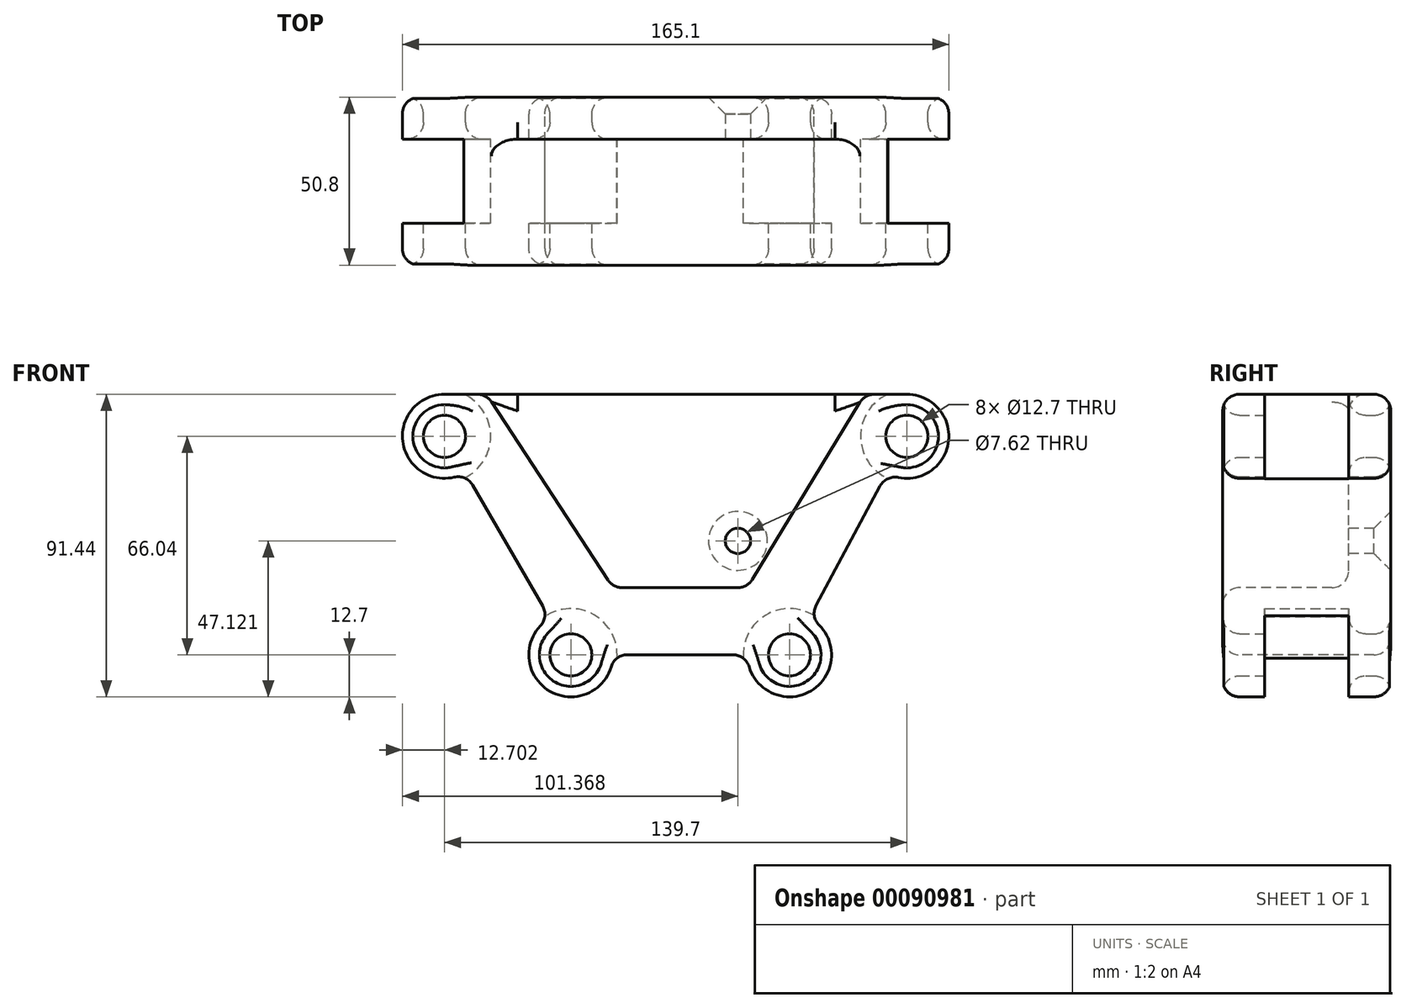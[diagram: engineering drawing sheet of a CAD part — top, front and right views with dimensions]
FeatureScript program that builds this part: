
annotation { "Feature Type Name" : "Feature", "Feature Type Description" : "" }
export const myFeature = defineFeature(function(context is Context, id is Id, definition is map)
    precondition{}
    {
        {
            var Q0;
            Q0=qCreatedBy(makeId("Front.planeOp"),FACE);
            var sketch = newSketch(context, id + "F0", { "sketchPlane" : qUnion([Q0])});
            skLineSegment(sketch, "E0", {"start": v(-31.21, -66.04) * mm, "end": v(34.83, -66.04) * mm});
            skLineSegment(sketch, "E1", {"start": v(34.83, -66.04) * mm, "end": v(70.3, 0) * mm});
            skLineSegment(sketch, "E2", {"start": v(-31.21, -66.04) * mm, "end": v(-69.4, 0) * mm});
            skCircle(sketch, "E3", {"center": v(-69.4, 0) * mm, "radius": 6.35 * mm});
            skCircle(sketch, "E4", {"center": v(-31.21, -66.04) * mm, "radius": 6.35 * mm});
            skCircle(sketch, "E5", {"center": v(34.83, -66.04) * mm, "radius": 6.35 * mm});
            skCircle(sketch, "E6", {"center": v(70.3, 0) * mm, "radius": 6.35 * mm});
            skCircle(sketch, "E7", {"center": v(-69.4, 0) * mm, "radius": 12.7 * mm});
            skCircle(sketch, "E8", {"center": v(-31.21, -66.04) * mm, "radius": 12.7 * mm});
            skCircle(sketch, "E9", {"center": v(34.83, -66.04) * mm, "radius": 12.7 * mm});
            skCircle(sketch, "E10", {"center": v(70.3, 0) * mm, "radius": 12.7 * mm});
            skLineSegment(sketch, "E11", {"start": v(-69.4, 12.7) * mm, "end": v(70.3, 12.7) * mm});
            skLineSegment(sketch, "E12", {"start": v(1.8, -66.04) * mm, "end": v(1.8, -31.77) * mm, "construction": true});
            skPoint(sketch, "E13", {"position": v(1.8, 12.7) * mm});
            skSolve(sketch);
        }
        {
            var Q0;
            Q0 = qSketchRegion(id + "F0", true);
            extrude(context, id + "F1", {"entities" : qUnion([Q0]), "endBound" : BoundingType.SYMMETRIC, "depth" : 50.8 * mm});
        }
        {
            var Q0;
            Q0=makeQuery(id+"F1.opExtrude","CAP_FACE",FACE,{"disambiguationData":[OSD([sQuery(id+"F0.wireOp",EDGE,"E0"),sQuery(id+"F0.wireOp",EDGE,"E1"),sQuery(id+"F0.wireOp",EDGE,"E2"),sQuery(id+"F0.wireOp",EDGE,"E3"),sQuery(id+"F0.wireOp",EDGE,"E4"),sQuery(id+"F0.wireOp",EDGE,"E5"),sQuery(id+"F0.wireOp",EDGE,"E6"),sQuery(id+"F0.wireOp",EDGE,"E7"),sQuery(id+"F0.wireOp",EDGE,"E8"),sQuery(id+"F0.wireOp",EDGE,"E9"),sQuery(id+"F0.wireOp",EDGE,"E10"),sQuery(id+"F0.wireOp",EDGE,"E11")])],"isStart":false});
            var sketch = newSketch(context, id + "F2", { "sketchPlane" : qUnion([Q0])});
            skLineSegment(sketch, "E14", {"start": v(-18.51, -45.72) * mm, "end": v(22.13, -45.72) * mm});
            skLineSegment(sketch, "E15", {"start": v(22.13, -45.72) * mm, "end": v(57.6, 12.7) * mm});
            skLineSegment(sketch, "E16", {"start": v(57.6, 12.7) * mm, "end": v(-56.7, 12.7) * mm});
            skLineSegment(sketch, "E17", {"start": v(-56.7, 12.7) * mm, "end": v(-18.51, -45.72) * mm});
            skSolve(sketch);
        }
        {
            var Q0;
            Q0 = qSketchRegion(id + "F2", true);
            extrude(context, id + "F3", {"entities" : qUnion([Q0]), "operationType" : NewBodyOperationType.REMOVE, "oppositeDirection" : true, "depth" : 38.1 * mm});
        }
        {
            var Q0;
            Q0=makeQuery(id+"F1.opExtrude","SWEPT_FACE",FACE,{"disambiguationData":[OSD([sQuery(id+"F0.wireOp",EDGE,"E1")])]});
            var Q1;
            Q1=makeQuery(id+"F1.opExtrude","SWEPT_FACE",FACE,{"disambiguationData":[OSD([sQuery(id+"F0.wireOp",EDGE,"E2")])]});
            var Q2;
            Q2=makeQuery(id+"F1.opExtrude","SWEPT_FACE",FACE,{"disambiguationData":[OSD([sQuery(id+"F0.wireOp",EDGE,"E5")])]});
            var Q3;
            Q3=makeQuery(id+"F1.opExtrude","CAP_EDGE",EDGE,{"disambiguationData":[OSD([sQuery(id+"F0.wireOp",EDGE,"E6")])],"isStart":false});
            var Q4;
            Q4=makeQuery(id+"F1.opExtrude","SWEPT_FACE",FACE,{"disambiguationData":[OSD([sQuery(id+"F0.wireOp",EDGE,"E8")])]});
            var Q5;
            Q5=makeQuery(id+"F1.opExtrude","CAP_EDGE",EDGE,{"disambiguationData":[OSD([sQuery(id+"F0.wireOp",EDGE,"E9")])],"isStart":true});
            var Q6;
            Q6=makeQuery(id+"F3.boolean.opBoolean","COPY",EDGE,{"derivedFrom":makeQuery(id+"F3.opExtrude","CAP_EDGE",EDGE,{"disambiguationData":[OSD([sQuery(id+"F2.wireOp",EDGE,"E17")])],"isStart":false})});
            var Q7;
            Q7=makeQuery(id+"F3.boolean.opBoolean","COPY",EDGE,{"derivedFrom":makeQuery(id+"F3.opExtrude","CAP_EDGE",EDGE,{"disambiguationData":[OSD([sQuery(id+"F2.wireOp",EDGE,"E17")])],"isStart":true})});
            var Q8;
            Q8=makeQuery(id+"F1.opExtrude","CAP_EDGE",EDGE,{"disambiguationData":[OSD([sQuery(id+"F0.wireOp",EDGE,"E8")])],"isStart":false});
            var Q9;
            Q9=makeQuery(id+"F1.opExtrude","SWEPT_FACE",FACE,{"disambiguationData":[OSD([sQuery(id+"F0.wireOp",EDGE,"E9")])]});
            var Q10;
            Q10=makeQuery(id+"F1.opExtrude","CAP_EDGE",EDGE,{"disambiguationData":[OSD([sQuery(id+"F0.wireOp",EDGE,"E10")])],"isStart":false});
            var Q11;
            Q11=makeQuery(id+"F3.boolean.opBoolean","COPY",FACE,{"derivedFrom":makeQuery(id+"F3.opExtrude","SWEPT_FACE",FACE,{"disambiguationData":[OSD([sQuery(id+"F2.wireOp",EDGE,"E14")])]})});
            var Q12;
            Q12=makeQuery(id+"F1.opExtrude","CAP_EDGE",EDGE,{"disambiguationData":[OSD([sQuery(id+"F0.wireOp",EDGE,"E2")])],"isStart":false});
            var Q13;
            Q13=makeQuery(id+"F1.opExtrude","CAP_EDGE",EDGE,{"disambiguationData":[OSD([sQuery(id+"F0.wireOp",EDGE,"E5")])],"isStart":false});
            var Q14;
            Q14=makeQuery(id+"F1.opExtrude","CAP_EDGE",EDGE,{"disambiguationData":[OSD([sQuery(id+"F0.wireOp",EDGE,"E1")])],"isStart":true});
            var Q15;
            Q15=makeQuery(id+"F3.boolean.opBoolean","COPY",FACE,{"derivedFrom":makeQuery(id+"F3.opExtrude","CAP_FACE",FACE,{"disambiguationData":[OSD([sQuery(id+"F2.wireOp",EDGE,"E14"),sQuery(id+"F2.wireOp",EDGE,"E15"),sQuery(id+"F2.wireOp",EDGE,"E16"),sQuery(id+"F2.wireOp",EDGE,"E17")])],"isStart":false})});
            var Q16;
            Q16=makeQuery(id+"F1.opExtrude","SWEPT_FACE",FACE,{"disambiguationData":[OSD([sQuery(id+"F0.wireOp",EDGE,"E6")])]});
            var Q17;
            Q17=makeQuery(id+"F1.opExtrude","SWEPT_FACE",FACE,{"disambiguationData":[OSD([sQuery(id+"F0.wireOp",EDGE,"E3")])]});
            var Q18;
            Q18=makeQuery(id+"F1.opExtrude","CAP_FACE",FACE,{"disambiguationData":[OSD([sQuery(id+"F0.wireOp",EDGE,"E0"),sQuery(id+"F0.wireOp",EDGE,"E1"),sQuery(id+"F0.wireOp",EDGE,"E2"),sQuery(id+"F0.wireOp",EDGE,"E3"),sQuery(id+"F0.wireOp",EDGE,"E4"),sQuery(id+"F0.wireOp",EDGE,"E5"),sQuery(id+"F0.wireOp",EDGE,"E6"),sQuery(id+"F0.wireOp",EDGE,"E7"),sQuery(id+"F0.wireOp",EDGE,"E8"),sQuery(id+"F0.wireOp",EDGE,"E9"),sQuery(id+"F0.wireOp",EDGE,"E10"),sQuery(id+"F0.wireOp",EDGE,"E11")])],"isStart":true});
            var Q19;
            Q19=makeQuery(id+"F1.opExtrude","CAP_EDGE",EDGE,{"disambiguationData":[OSD([sQuery(id+"F0.wireOp",EDGE,"E3")])],"isStart":false});
            var Q20;
            Q20=makeQuery(id+"F1.opExtrude","SWEPT_FACE",FACE,{"disambiguationData":[OSD([sQuery(id+"F0.wireOp",EDGE,"E7")])]});
            var Q21;
            Q21=makeQuery(id+"F1.opExtrude","CAP_EDGE",EDGE,{"disambiguationData":[OSD([sQuery(id+"F0.wireOp",EDGE,"E4")])],"isStart":false});
            var Q22;
            Q22=makeQuery(id+"F1.opExtrude","SWEPT_FACE",FACE,{"disambiguationData":[OSD([sQuery(id+"F0.wireOp",EDGE,"E4")])]});
            var Q23;
            Q23=makeQuery(id+"F1.opExtrude","SWEPT_FACE",FACE,{"disambiguationData":[OSD([sQuery(id+"F0.wireOp",EDGE,"E0")])]});
            var Q24;
            Q24=makeQuery(id+"F3.boolean.opBoolean","COPY",EDGE,{"derivedFrom":makeQuery(id+"F3.opExtrude","SWEPT_EDGE",EDGE,{"disambiguationData":[OSD([sQuery(id+"F0.wireOp",EDGE,"E11"),sQuery(id+"F2.wireOp",EDGE,"E16"),sQuery(id+"F2.wireOp",EDGE,"E17")])]})});
            var Q25;
            Q25=makeQuery(id+"F1.opExtrude","CAP_EDGE",EDGE,{"disambiguationData":[OSD([sQuery(id+"F0.wireOp",EDGE,"E9")])],"isStart":false});
            var Q26;
            Q26=makeQuery(id+"F1.opExtrude","CAP_EDGE",EDGE,{"disambiguationData":[OSD([sQuery(id+"F0.wireOp",EDGE,"E10")])],"isStart":true});
            var Q27;
            Q27=makeQuery(id+"F1.opExtrude","SWEPT_FACE",FACE,{"disambiguationData":[OSD([sQuery(id+"F0.wireOp",EDGE,"E10")])]});
            var Q28;
            Q28=makeQuery(id+"F1.opExtrude","CAP_FACE",FACE,{"disambiguationData":[OSD([sQuery(id+"F0.wireOp",EDGE,"E0"),sQuery(id+"F0.wireOp",EDGE,"E1"),sQuery(id+"F0.wireOp",EDGE,"E2"),sQuery(id+"F0.wireOp",EDGE,"E3"),sQuery(id+"F0.wireOp",EDGE,"E4"),sQuery(id+"F0.wireOp",EDGE,"E5"),sQuery(id+"F0.wireOp",EDGE,"E6"),sQuery(id+"F0.wireOp",EDGE,"E7"),sQuery(id+"F0.wireOp",EDGE,"E8"),sQuery(id+"F0.wireOp",EDGE,"E9"),sQuery(id+"F0.wireOp",EDGE,"E10"),sQuery(id+"F0.wireOp",EDGE,"E11")])],"isStart":false});
            var Q29;
            Q29=makeQuery(id+"F3.boolean.opBoolean","COPY",FACE,{"derivedFrom":makeQuery(id+"F3.opExtrude","SWEPT_FACE",FACE,{"disambiguationData":[OSD([sQuery(id+"F2.wireOp",EDGE,"E15")])]})});
            var Q30;
            Q30=makeQuery(id+"F3.boolean.opBoolean","COPY",EDGE,{"derivedFrom":makeQuery(id+"F3.opExtrude","CAP_EDGE",EDGE,{"disambiguationData":[OSD([sQuery(id+"F2.wireOp",EDGE,"E15")])],"isStart":true})});
            var Q31;
            Q31=makeQuery(id+"F3.boolean.opBoolean","COPY",EDGE,{"derivedFrom":makeQuery(id+"F3.opExtrude","CAP_EDGE",EDGE,{"disambiguationData":[OSD([sQuery(id+"F2.wireOp",EDGE,"E16")])],"isStart":false})});
            var Q32;
            Q32=makeQuery(id+"F1.opExtrude","SWEPT_FACE",FACE,{"disambiguationData":[OSD([sQuery(id+"F0.wireOp",EDGE,"E11")])]});
            var Q33;
            Q33=makeQuery(id+"F1.opExtrude","CAP_EDGE",EDGE,{"disambiguationData":[OSD([sQuery(id+"F0.wireOp",EDGE,"E7")])],"isStart":false});
            var Q34;
            Q34=makeQuery(id+"F1.opExtrude","CAP_EDGE",EDGE,{"disambiguationData":[OSD([sQuery(id+"F0.wireOp",EDGE,"E1")])],"isStart":false});
            var Q35;
            Q35=makeQuery(id+"F3.boolean.opBoolean","COPY",FACE,{"derivedFrom":makeQuery(id+"F3.opExtrude","SWEPT_FACE",FACE,{"disambiguationData":[OSD([sQuery(id+"F2.wireOp",EDGE,"E17")])]})});
            var Q36;
            Q36=makeQuery(id+"F1.opExtrude","SWEPT_EDGE",EDGE,{"disambiguationData":[OSD([sQuery(id+"F0.wireOp",EDGE,"E10"),sQuery(id+"F0.wireOp",EDGE,"E11")])]});
            var Q37;
            Q37=makeQuery(id+"F1.opExtrude","SWEPT_EDGE",EDGE,{"disambiguationData":[OSD([sQuery(id+"F0.wireOp",EDGE,"E1"),sQuery(id+"F0.wireOp",EDGE,"E10")])]});
            var Q38;
            Q38=makeQuery(id+"F1.opExtrude","CAP_EDGE",EDGE,{"disambiguationData":[OSD([sQuery(id+"F0.wireOp",EDGE,"E4")])],"isStart":true});
            var Q39;
            Q39=makeQuery(id+"F1.opExtrude","CAP_EDGE",EDGE,{"disambiguationData":[OSD([sQuery(id+"F0.wireOp",EDGE,"E6")])],"isStart":true});
            var Q40;
            Q40=makeQuery(id+"F3.boolean.opBoolean","COPY",EDGE,{"derivedFrom":makeQuery(id+"F3.opExtrude","SWEPT_EDGE",EDGE,{"disambiguationData":[OSD([sQuery(id+"F0.wireOp",EDGE,"E11"),sQuery(id+"F2.wireOp",EDGE,"E15"),sQuery(id+"F2.wireOp",EDGE,"E16")])]})});
            var Q41;
            Q41=makeQuery(id+"F1.opExtrude","CAP_EDGE",EDGE,{"disambiguationData":[OSD([sQuery(id+"F0.wireOp",EDGE,"E7")])],"isStart":true});
            var Q42;
            Q42=makeQuery(id+"F3.boolean.opBoolean","COPY",EDGE,{"derivedFrom":makeQuery(id+"F3.opExtrude","SWEPT_EDGE",EDGE,{"disambiguationData":[OSD([sQuery(id+"F2.wireOp",EDGE,"E14"),sQuery(id+"F2.wireOp",EDGE,"E17")])]})});
            var Q43;
            Q43=makeQuery(id+"F1.opExtrude","CAP_EDGE",EDGE,{"disambiguationData":[OSD([sQuery(id+"F0.wireOp",EDGE,"E2")])],"isStart":true});
            var Q44;
            Q44=makeQuery(id+"F1.opExtrude","CAP_EDGE",EDGE,{"disambiguationData":[OSD([sQuery(id+"F0.wireOp",EDGE,"E0")])],"isStart":false});
            var Q45;
            Q45=makeQuery(id+"F1.opExtrude","CAP_EDGE",EDGE,{"disambiguationData":[OSD([sQuery(id+"F0.wireOp",EDGE,"E11")])],"isStart":true});
            var Q46;
            Q46=makeQuery(id+"F1.opExtrude","CAP_EDGE",EDGE,{"disambiguationData":[OSD([sQuery(id+"F0.wireOp",EDGE,"E8")])],"isStart":true});
            var Q47;
            Q47=makeQuery(id+"F1.opExtrude","SWEPT_EDGE",EDGE,{"disambiguationData":[OSD([sQuery(id+"F0.wireOp",EDGE,"E2"),sQuery(id+"F0.wireOp",EDGE,"E7")])]});
            var Q48;
            Q48=makeQuery(id+"F1.opExtrude","SWEPT_EDGE",EDGE,{"disambiguationData":[OSD([sQuery(id+"F0.wireOp",EDGE,"E2"),sQuery(id+"F0.wireOp",EDGE,"E8")])]});
            var Q49;
            Q49=makeQuery(id+"F1.opExtrude","SWEPT_EDGE",EDGE,{"disambiguationData":[OSD([sQuery(id+"F0.wireOp",EDGE,"E7"),sQuery(id+"F0.wireOp",EDGE,"E11")])]});
            var Q50;
            Q50=makeQuery(id+"F1.opExtrude","CAP_EDGE",EDGE,{"disambiguationData":[OSD([sQuery(id+"F0.wireOp",EDGE,"E5")])],"isStart":true});
            var Q51;
            Q51=makeQuery(id+"F1.opExtrude","CAP_EDGE",EDGE,{"disambiguationData":[OSD([sQuery(id+"F0.wireOp",EDGE,"E3")])],"isStart":true});
            var Q52;
            Q52=makeQuery(id+"F1.opExtrude","SWEPT_EDGE",EDGE,{"disambiguationData":[OSD([sQuery(id+"F0.wireOp",EDGE,"E1"),sQuery(id+"F0.wireOp",EDGE,"E9")])]});
            var Q53;
            Q53=makeQuery(id+"F1.opExtrude","SWEPT_EDGE",EDGE,{"disambiguationData":[OSD([sQuery(id+"F0.wireOp",EDGE,"E0"),sQuery(id+"F0.wireOp",EDGE,"E9")])]});
            var Q54;
            Q54=makeQuery(id+"F1.opExtrude","SWEPT_EDGE",EDGE,{"disambiguationData":[OSD([sQuery(id+"F0.wireOp",EDGE,"E0"),sQuery(id+"F0.wireOp",EDGE,"E8")])]});
            var Q55;
            Q55=makeQuery(id+"F3.boolean.opBoolean","COPY",EDGE,{"derivedFrom":makeQuery(id+"F3.opExtrude","CAP_EDGE",EDGE,{"disambiguationData":[OSD([sQuery(id+"F2.wireOp",EDGE,"E15")])],"isStart":false})});
            var Q56;
            {var subQ0=sQuery(id+"F0.wireOp",EDGE,"E11");var subQ1=sQuery(id+"F0.wireOp",EDGE,"E7");Q56=makeQuery(id+"F3.boolean.opBoolean","SPLIT",EDGE,{"disambiguationData":[TD([makeQuery(id+"F1.opExtrude","SWEPT_FACE",FACE,{"disambiguationData":[OSD([subQ1])]})])],"derivedFrom":makeQuery(id+"F1.opExtrude","CAP_EDGE",EDGE,{"disambiguationData":[OSD([subQ0])],"isStart":false})});}
            var Q57;
            Q57=makeQuery(id+"F3.boolean.opBoolean","COPY",EDGE,{"derivedFrom":makeQuery(id+"F3.opExtrude","CAP_EDGE",EDGE,{"disambiguationData":[OSD([sQuery(id+"F2.wireOp",EDGE,"E14")])],"isStart":true})});
            var Q58;
            {var subQ0=sQuery(id+"F0.wireOp",EDGE,"E11");var subQ1=sQuery(id+"F0.wireOp",EDGE,"E10");Q58=makeQuery(id+"F3.boolean.opBoolean","SPLIT",EDGE,{"disambiguationData":[TD([makeQuery(id+"F1.opExtrude","SWEPT_FACE",FACE,{"disambiguationData":[OSD([subQ1])]})])],"derivedFrom":makeQuery(id+"F1.opExtrude","CAP_EDGE",EDGE,{"disambiguationData":[OSD([subQ0])],"isStart":false})});}
            var Q59;
            Q59=makeQuery(id+"F3.boolean.opBoolean","COPY",EDGE,{"derivedFrom":makeQuery(id+"F3.opExtrude","SWEPT_EDGE",EDGE,{"disambiguationData":[OSD([sQuery(id+"F2.wireOp",EDGE,"E14"),sQuery(id+"F2.wireOp",EDGE,"E15")])]})});
            var Q60;
            Q60=makeQuery(id+"F1.opExtrude","CAP_EDGE",EDGE,{"disambiguationData":[OSD([sQuery(id+"F0.wireOp",EDGE,"E0")])],"isStart":true});
            var Q61;
            Q61=makeQuery(id+"F3.boolean.opBoolean","COPY",EDGE,{"derivedFrom":makeQuery(id+"F3.opExtrude","CAP_EDGE",EDGE,{"disambiguationData":[OSD([sQuery(id+"F2.wireOp",EDGE,"E14")])],"isStart":false})});
            fillet(context, id + "F4", {"entities" : qUnion([Q0, Q1, Q2, Q3, Q4, Q5, Q6, Q7, Q8, Q9, Q10, Q11, Q12, Q13, Q14, Q15, Q16, Q17, Q18, Q19, Q20, Q21, Q22, Q23, Q24, Q25, Q26, Q27, Q28, Q29, Q30, Q31, Q32, Q33, Q34, Q35, Q36, Q37, Q38, Q39, Q40, Q41, Q42, Q43, Q44, Q45, Q46, Q47, Q48, Q49, Q50, Q51, Q52, Q53, Q54, Q55, Q56, Q57, Q58, Q59, Q60, Q61]), "radius" : 5.08 * mm, "tangentPropagation" : true, "allowEdgeOverflow" : false});
        }
        {
            var Q0;
            Q0=qCreatedBy(makeId("Front.planeOp"),FACE);
            var sketch = newSketch(context, id + "F5", { "sketchPlane" : qUnion([Q0])});
            skCircle(sketch, "E18.0", {"center": v(-69.4, 0) * mm, "radius": 6.35 * mm});
            skCircle(sketch, "E19.0", {"center": v(70.3, 0) * mm, "radius": 6.35 * mm});
            skCircle(sketch, "E20.0", {"center": v(34.83, -66.04) * mm, "radius": 6.35 * mm});
            skCircle(sketch, "E21.0", {"center": v(-31.21, -66.04) * mm, "radius": 6.35 * mm});
            skCircle(sketch, "E22", {"center": v(-69.4, 0) * mm, "radius": 13.97 * mm});
            skCircle(sketch, "E23", {"center": v(70.3, 0) * mm, "radius": 13.97 * mm});
            skCircle(sketch, "E24", {"center": v(-31.21, -66.04) * mm, "radius": 13.97 * mm});
            skCircle(sketch, "E25", {"center": v(34.83, -66.04) * mm, "radius": 13.97 * mm});
            skSolve(sketch);
        }
        {
            var Q0;
            Q0 = qSketchRegion(id + "F5", true);
            extrude(context, id + "F6", {"entities" : qUnion([Q0]), "operationType" : NewBodyOperationType.REMOVE, "endBound" : BoundingType.SYMMETRIC, "depth" : 25.4 * mm});
        }
        {
            var Q0;
            Q0=makeQuery(id+"F3.boolean.opBoolean","COPY",FACE,{"derivedFrom":makeQuery(id+"F3.opExtrude","CAP_FACE",FACE,{"disambiguationData":[OSD([sQuery(id+"F2.wireOp",EDGE,"E14"),sQuery(id+"F2.wireOp",EDGE,"E15"),sQuery(id+"F2.wireOp",EDGE,"E16"),sQuery(id+"F2.wireOp",EDGE,"E17")])],"isStart":false})});
            var sketch = newSketch(context, id + "F7", { "sketchPlane" : qUnion([Q0])});
            skLineSegment(sketch, "E26", {"start": v(0, -31.62) * mm, "end": v(-27.73, -31.62) * mm});
            skLineSegment(sketch, "E27", {"start": v(-27.73, -31.62) * mm, "end": v(30.69, -31.62) * mm});
            skCircle(sketch, "E28", {"center": v(-16.3, -31.62) * mm, "radius": 3.81 * mm});
            skCircle(sketch, "E29", {"center": v(19.26, -31.62) * mm, "radius": 3.81 * mm});
            skSolve(sketch);
        }
        {
            var Q0;
            {var subQ0=sQuery(id+"F7.wireOp",EDGE,"E28");var subQ1=sQuery(id+"F7.wireOp",EDGE,"E27");var subQ2=makeQuery(id+"F7.imprint","INTERSECT",VERTEX,{"disambiguationData":[OD(0.0)],"derivedFrom":[subQ1,subQ0]});Q0=makeQuery(id+"F7.imprint","IMPRINT",FACE,{"disambiguationData":[TD([[makeQuery(id+"F7.imprint","IMPRINT",EDGE,{"disambiguationData":[TD([[subQ2,-1.0]])],"derivedFrom":subQ1}),-1.0]])]});}
            var Q1;
            {var subQ0=sQuery(id+"F7.wireOp",EDGE,"E29");var subQ1=sQuery(id+"F7.wireOp",EDGE,"E27");var subQ2=makeQuery(id+"F7.imprint","INTERSECT",VERTEX,{"disambiguationData":[OD(0.0)],"derivedFrom":[subQ1,subQ0]});Q1=makeQuery(id+"F7.imprint","IMPRINT",FACE,{"disambiguationData":[TD([[makeQuery(id+"F7.imprint","IMPRINT",EDGE,{"disambiguationData":[TD([[subQ2,-1.0]])],"derivedFrom":subQ1}),-1.0]])]});}
            var Q2;
            {var subQ0=sQuery(id+"F7.wireOp",EDGE,"E28");var subQ1=sQuery(id+"F7.wireOp",EDGE,"E27");var subQ2=makeQuery(id+"F7.imprint","INTERSECT",VERTEX,{"disambiguationData":[OD(0.0)],"derivedFrom":[subQ1,subQ0]});Q2=makeQuery(id+"F7.imprint","IMPRINT",FACE,{"disambiguationData":[TD([[makeQuery(id+"F7.imprint","IMPRINT",EDGE,{"disambiguationData":[TD([[subQ2,-1.0]])],"derivedFrom":subQ1}),1.0]])]});}
            var Q3;
            {var subQ0=sQuery(id+"F7.wireOp",EDGE,"E29");var subQ1=sQuery(id+"F7.wireOp",EDGE,"E27");var subQ2=makeQuery(id+"F7.imprint","INTERSECT",VERTEX,{"disambiguationData":[OD(0.0)],"derivedFrom":[subQ1,subQ0]});Q3=makeQuery(id+"F7.imprint","IMPRINT",FACE,{"disambiguationData":[TD([[makeQuery(id+"F7.imprint","IMPRINT",EDGE,{"disambiguationData":[TD([[subQ2,-1.0]])],"derivedFrom":subQ1}),1.0]])]});}
            var Q4;
            Q4=sQuery(id+"F7.wireOp",EDGE,"E28");
            var Q5;
            Q5=sQuery(id+"F7.wireOp",EDGE,"E29");
            extrude(context, id + "F8", {"entities" : qUnion([Q0, Q1, Q2, Q3]), "operationType" : NewBodyOperationType.REMOVE, "surfaceEntities" : qUnion([Q4, Q5]), "oppositeDirection" : true, "depth" : 76.2 * mm});
        }
        {
            var Q0;
            Q0=makeQuery(id+"F6.boolean.opBoolean","COPY",EDGE,{"derivedFrom":makeQuery(id+"F6.opExtrude","CAP_EDGE",EDGE,{"disambiguationData":[OSD([sQuery(id+"F5.wireOp",EDGE,"E19.0")])],"isStart":false})});
            var Q1;
            Q1=makeQuery(id+"F6.boolean.opBoolean","COPY",EDGE,{"derivedFrom":makeQuery(id+"F6.opExtrude","CAP_EDGE",EDGE,{"disambiguationData":[OSD([sQuery(id+"F5.wireOp",EDGE,"E20.0")])],"isStart":false})});
            var Q2;
            Q2=makeQuery(id+"F6.boolean.opBoolean","COPY",EDGE,{"derivedFrom":makeQuery(id+"F6.opExtrude","CAP_EDGE",EDGE,{"disambiguationData":[OSD([sQuery(id+"F5.wireOp",EDGE,"E19.0")])],"isStart":true})});
            var Q3;
            Q3=makeQuery(id+"F6.boolean.opBoolean","COPY",EDGE,{"derivedFrom":makeQuery(id+"F6.opExtrude","CAP_EDGE",EDGE,{"disambiguationData":[OSD([sQuery(id+"F5.wireOp",EDGE,"E20.0")])],"isStart":true})});
            var Q4;
            Q4=makeQuery(id+"F6.boolean.opBoolean","COPY",EDGE,{"derivedFrom":makeQuery(id+"F6.opExtrude","CAP_EDGE",EDGE,{"disambiguationData":[OSD([sQuery(id+"F5.wireOp",EDGE,"E18.0")])],"isStart":true})});
            var Q5;
            Q5=makeQuery(id+"F6.boolean.opBoolean","COPY",EDGE,{"derivedFrom":makeQuery(id+"F6.opExtrude","CAP_EDGE",EDGE,{"disambiguationData":[OSD([sQuery(id+"F5.wireOp",EDGE,"E21.0")])],"isStart":true})});
            var Q6;
            Q6=makeQuery(id+"F6.boolean.opBoolean","COPY",EDGE,{"derivedFrom":makeQuery(id+"F6.opExtrude","CAP_EDGE",EDGE,{"disambiguationData":[OSD([sQuery(id+"F5.wireOp",EDGE,"E18.0")])],"isStart":false})});
            var Q7;
            Q7=makeQuery(id+"F6.boolean.opBoolean","COPY",EDGE,{"derivedFrom":makeQuery(id+"F6.opExtrude","CAP_EDGE",EDGE,{"disambiguationData":[OSD([sQuery(id+"F5.wireOp",EDGE,"E21.0")])],"isStart":false})});
            fillet(context, id + "F9", {"entities" : qUnion([Q0, Q1, Q2, Q3, Q4, Q5, Q6, Q7]), "radius" : 5.08 * mm, "tangentPropagation" : true, "allowEdgeOverflow" : false});
        }
        {
            var Q0;
            Q0=makeQuery(id+"F8.boolean.opBoolean","INTERSECT",EDGE,{"derivedFrom":[makeQuery(id+"F1.opExtrude","CAP_FACE",FACE,{"disambiguationData":[OSD([sQuery(id+"F0.wireOp",EDGE,"E0"),sQuery(id+"F0.wireOp",EDGE,"E1"),sQuery(id+"F0.wireOp",EDGE,"E2"),sQuery(id+"F0.wireOp",EDGE,"E3"),sQuery(id+"F0.wireOp",EDGE,"E4"),sQuery(id+"F0.wireOp",EDGE,"E5"),sQuery(id+"F0.wireOp",EDGE,"E6"),sQuery(id+"F0.wireOp",EDGE,"E7"),sQuery(id+"F0.wireOp",EDGE,"E8"),sQuery(id+"F0.wireOp",EDGE,"E9"),sQuery(id+"F0.wireOp",EDGE,"E10"),sQuery(id+"F0.wireOp",EDGE,"E11")])],"isStart":true}),makeQuery(id+"F8.opExtrude","SWEPT_FACE",FACE,{"disambiguationData":[OSD([sQuery(id+"F7.wireOp",EDGE,"E28")])]})]});
            var Q1;
            Q1=makeQuery(id+"F8.boolean.opBoolean","INTERSECT",EDGE,{"derivedFrom":[makeQuery(id+"F1.opExtrude","CAP_FACE",FACE,{"disambiguationData":[OSD([sQuery(id+"F0.wireOp",EDGE,"E0"),sQuery(id+"F0.wireOp",EDGE,"E1"),sQuery(id+"F0.wireOp",EDGE,"E2"),sQuery(id+"F0.wireOp",EDGE,"E3"),sQuery(id+"F0.wireOp",EDGE,"E4"),sQuery(id+"F0.wireOp",EDGE,"E5"),sQuery(id+"F0.wireOp",EDGE,"E6"),sQuery(id+"F0.wireOp",EDGE,"E7"),sQuery(id+"F0.wireOp",EDGE,"E8"),sQuery(id+"F0.wireOp",EDGE,"E9"),sQuery(id+"F0.wireOp",EDGE,"E10"),sQuery(id+"F0.wireOp",EDGE,"E11")])],"isStart":true}),makeQuery(id+"F8.opExtrude","SWEPT_FACE",FACE,{"disambiguationData":[OSD([sQuery(id+"F7.wireOp",EDGE,"E29")])]})]});
            chamfer(context, id + "F10", {"entities" : qUnion([Q0, Q1]), "width" : 5.08 * mm, "tangentPropagation" : true});
        }
    });
